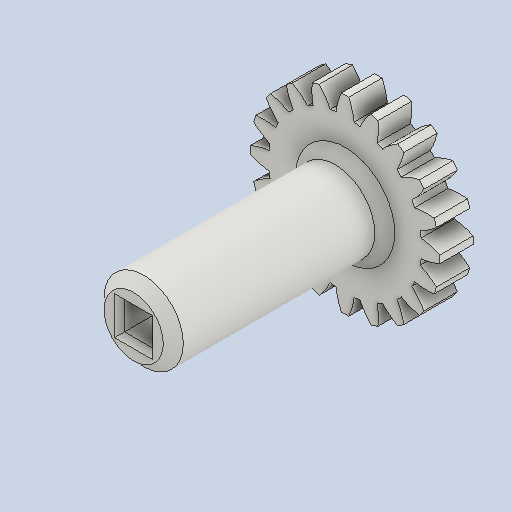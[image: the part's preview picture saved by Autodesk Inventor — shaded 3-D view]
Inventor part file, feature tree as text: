
AUTODESK INVENTOR PART (.ipt)
format: ipt  version: 2022 (Build 260153000, 153)  size: 547,840 bytes
history: native  units: mm (DEFAULTED — no unit token found)
features: sketch x4, extrude x3, plane x3, other x3, chamfer x2
ambient origin geometry x8: Origin, YZ Plane, XZ Plane, XY Plane, X Axis, Y Axis, Z Axis, Center Point
bodies: Solid1 (feature_tree)
feature tree (15):
  extrude  "Extrusion1"  Depth=4.0mm TaperAngle=0.0deg
  plane  "Work Plane1"
  plane  "Work Plane2"
  plane  "Work Plane3"
  other  "Spur Gear"
  extrude  "Extrusion2"  Depth=76.2mm TaperAngle=0.0deg
  extrude  "Extrusion3"  TaperAngle=0.0deg  [1 undecoded]
  chamfer  "Chamfer1"  Distance=25.4mm
  chamfer  "Chamfer2"  [1 undecoded]
  sketch  "Sketch1"  dims[d0=22.8mm d1=4.0mm d2=0.0mm]
  sketch  "Sketch2"  dims[d3=20.0mm d4=76.2mm d5=0.0mm]
  other  "Srf1"
  sketch  "Sketch3"  dims[d6=0.0mm d7=1.570796mm d9=0.0mm]
  sketch  "Sketch4"  dims[d14=0.0mm d15=25.4mm d16=0.0mm d17=0.0mm d18=0.0mm d19=25.4mm d20=3.375mm d21=0.0mm d22=0.0mm d23=9.525mm d24=25.4mm d25=0.0mm d26=1.2mm d27=3.175mm d28=45.0deg d29=0.6mm d30=3.175mm d31=45.0deg]
  other  "Pitch Diameter"
note: 2 required parameter values undecoded (feature->parameter linkage not recoverable at this tier; creation-order binding heuristic only, values carry confidence <= 0.55)
